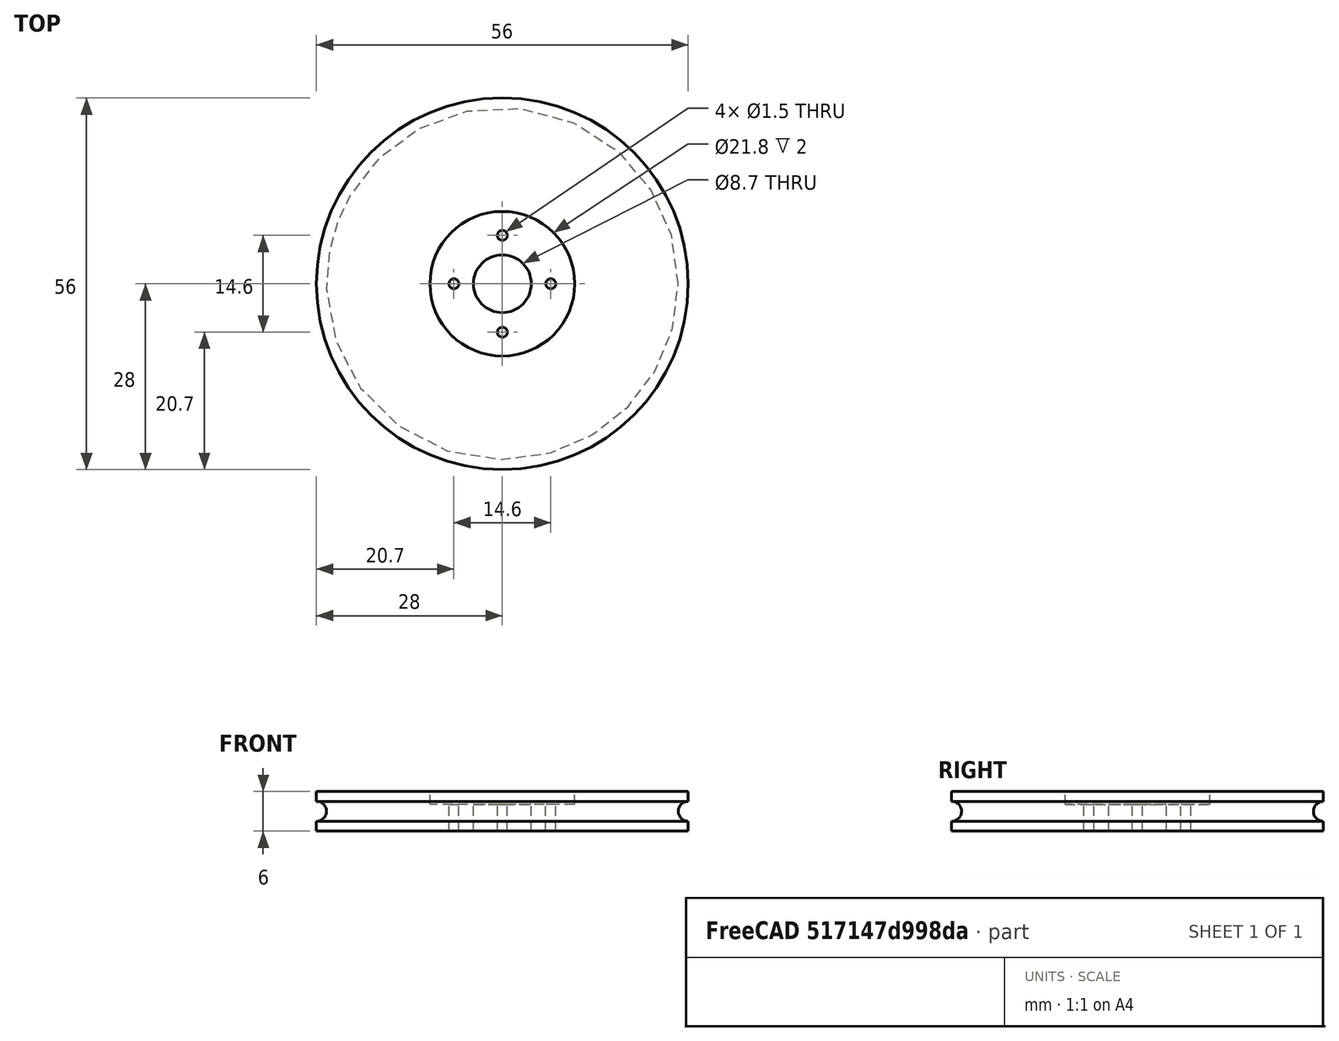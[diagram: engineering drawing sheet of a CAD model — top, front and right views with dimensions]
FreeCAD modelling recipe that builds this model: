
FCSTD DOCUMENT  (FreeCAD 0.18.4R)
Label: tutorial_freecad_ex15_a
License: All rights reserved
LicenseURL: http://en.wikipedia.org/wiki/All_rights_reserved
objects: Part::Cylinder×4, Part::Cut×4, Part::Torus×1, Part::FeaturePython×1
note: 10 computed .brp shape members not serialized (recipe doc carries the construction recipe); baked Part::Feature solids carry a one-line shape summary decoded from their .brp

FEATURE [Part::Cylinder] Cylinder  label="rueda_base"
  Angle = 360
  AttacherType = Attacher::AttachEngine3D
  Height = 6
  Placement = pos=(0,0,-3) rot=(0,0,1;0rad)
  Radius = 28
FEATURE [Part::Torus] Torus  label="hueco_torica"
  Angle1 = -180
  Angle2 = 180
  Angle3 = 360
  AttacherType = Attacher::AttachEngine3D
  Radius1 = 28
  Radius2 = 1.5
FEATURE [Part::Cut] Cut  label="rueda_basica"
  Base = -> Cylinder
  Refine = true
  Tool = -> Torus
FEATURE [Part::Cylinder] Cylinder001  label="Cilindro"
  Angle = 360
  AttacherType = Attacher::AttachEngine3D
  Height = 10
  Placement = pos=(0,0,1) rot=(0,0,1;0rad)
  Radius = 10.9
FEATURE [Part::Cut] Cut001  label="rueda_hueco_corona"
  Base = -> Cut
  Refine = true
  Tool = -> Cylinder001
FEATURE [Part::Cylinder] Cylinder002  label="hueco_eje"
  Angle = 360
  AttacherType = Attacher::AttachEngine3D
  Height = 10
  Placement = pos=(0,0,-5) rot=(0,0,1;-0.087266rad)
  Radius = 4.35
FEATURE [Part::Cut] Cut002  label="rueda_sin_taladros"
  Base = -> Cut001
  Refine = true
  Tool = -> Cylinder002
FEATURE [Part::Cylinder] Cylinder003  label="taladro"
  Angle = 360
  AttacherType = Attacher::AttachEngine3D
  Height = 10
  Placement = pos=(7.3,0,-5) rot=(0,0,1;0rad)
  Radius = 0.75
FEATURE [Part::FeaturePython] Array  # Draft array (typed FeaturePython)
  Angle = 360
  ArrayType = 1
  Axis = (0,0,1)
  Base = -> Cylinder003
  Center = (0,0,0)
  Fuse = false
  IntervalAxis = (0,0,0)
  IntervalX = (1,0,0)
  IntervalY = (0,1,0)
  IntervalZ = (0,0,1)
  NumberPolar = 4
  NumberX = 2
  NumberY = 2
  NumberZ = 1
FEATURE [Part::Cut] Cut003  label="rueda_Miniskybot"
  Base = -> Cut002
  Refine = true
  Tool = -> Array
